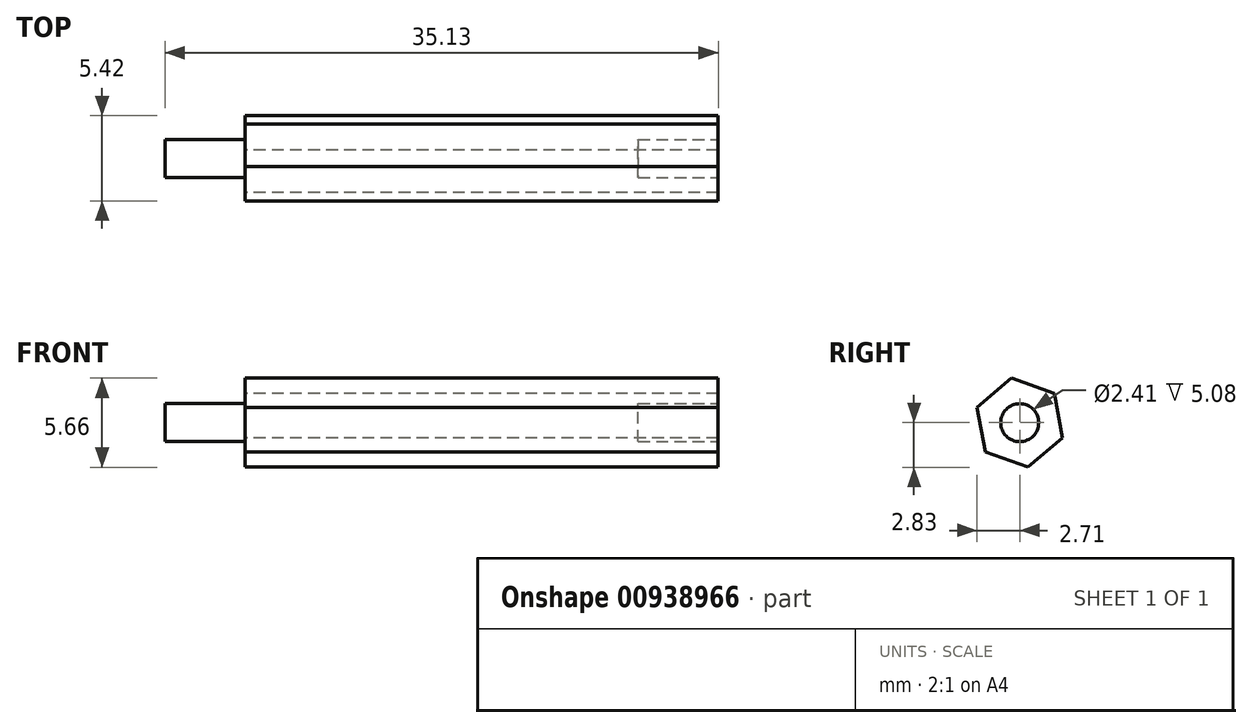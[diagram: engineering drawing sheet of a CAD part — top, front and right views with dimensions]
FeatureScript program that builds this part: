
annotation { "Feature Type Name" : "Feature", "Feature Type Description" : "" }
export const myFeature = defineFeature(function(context is Context, id is Id, definition is map)
    precondition{}
    {
        {
            var Q0;
            Q0=qCreatedBy(makeId("Right.planeOp"),FACE);
            var sketch = newSketch(context, id + "F0", { "sketchPlane" : qUnion([Q0])});
            skCircle(sketch, "E0.cCircle", {"center": v(0, 0) * mm, "radius": 2.49 * mm, "construction": true});
            skLineSegment(sketch, "E0.0", {"start": v(2.18, 1.87) * mm, "end": v(2.7, -0.96) * mm});
            skLineSegment(sketch, "E0.1", {"start": v(2.7, -0.96) * mm, "end": v(0.53, -2.83) * mm});
            skLineSegment(sketch, "E0.2", {"start": v(0.53, -2.83) * mm, "end": v(-2.18, -1.87) * mm});
            skLineSegment(sketch, "E0.3", {"start": v(-2.18, -1.87) * mm, "end": v(-2.7, 0.96) * mm});
            skLineSegment(sketch, "E0.4", {"start": v(-2.7, 0.96) * mm, "end": v(-0.53, 2.83) * mm});
            skLineSegment(sketch, "E0.5", {"start": v(-0.53, 2.83) * mm, "end": v(2.18, 1.87) * mm});
            skPoint(sketch, "E0.0.midPoint", {"position": v(2.45, 0.45) * mm});
            skSolve(sketch);
        }
        {
            var Q0;
            Q0=qSketchRegion(id+"F0",true);
            extrude(context, id + "F1", {"entities" : qUnion([Q0]), "depth" : 30.05 * mm});
        }
        {
            var Q0;
            Q0=makeQuery(id+"F1.opExtrude","CAP_FACE",FACE,{"disambiguationData":[OSD([sQuery(id+"F0.wireOp",EDGE,"E0.0"),sQuery(id+"F0.wireOp",EDGE,"E0.1"),sQuery(id+"F0.wireOp",EDGE,"E0.2"),sQuery(id+"F0.wireOp",EDGE,"E0.3"),sQuery(id+"F0.wireOp",EDGE,"E0.4"),sQuery(id+"F0.wireOp",EDGE,"E0.5")])],"isStart":true});
            var sketch = newSketch(context, id + "F2", { "sketchPlane" : qUnion([Q0])});
            skCircle(sketch, "E1", {"center": v(0, 0) * mm, "radius": 1.2 * mm});
            skSolve(sketch);
        }
        {
            var Q0;
            Q0=makeQuery(id+"F1.opExtrude","CAP_FACE",FACE,{"disambiguationData":[OSD([sQuery(id+"F0.wireOp",EDGE,"E0.0"),sQuery(id+"F0.wireOp",EDGE,"E0.1"),sQuery(id+"F0.wireOp",EDGE,"E0.2"),sQuery(id+"F0.wireOp",EDGE,"E0.3"),sQuery(id+"F0.wireOp",EDGE,"E0.4"),sQuery(id+"F0.wireOp",EDGE,"E0.5")])],"isStart":false});
            var sketch = newSketch(context, id + "F3", { "sketchPlane" : qUnion([Q0])});
            skCircle(sketch, "E2", {"center": v(0, 0) * mm, "radius": 1.2 * mm});
            skSolve(sketch);
        }
        {
            var Q0;
            Q0=qSketchRegion(id+"F3",true);
            var Q1;
            Q1=qSketchRegion(id+"F0",true);
            extrude(context, id + "F4", {"entities" : qUnion([Q0, Q1]), "operationType" : NewBodyOperationType.REMOVE, "oppositeDirection" : true, "depth" : 5.08 * mm});
        }
        {
            var Q0;
            Q0=qSketchRegion(id+"F2",true);
            extrude(context, id + "F5", {"entities" : qUnion([Q0]), "operationType" : NewBodyOperationType.ADD, "depth" : 5.08 * mm});
        }
    });
